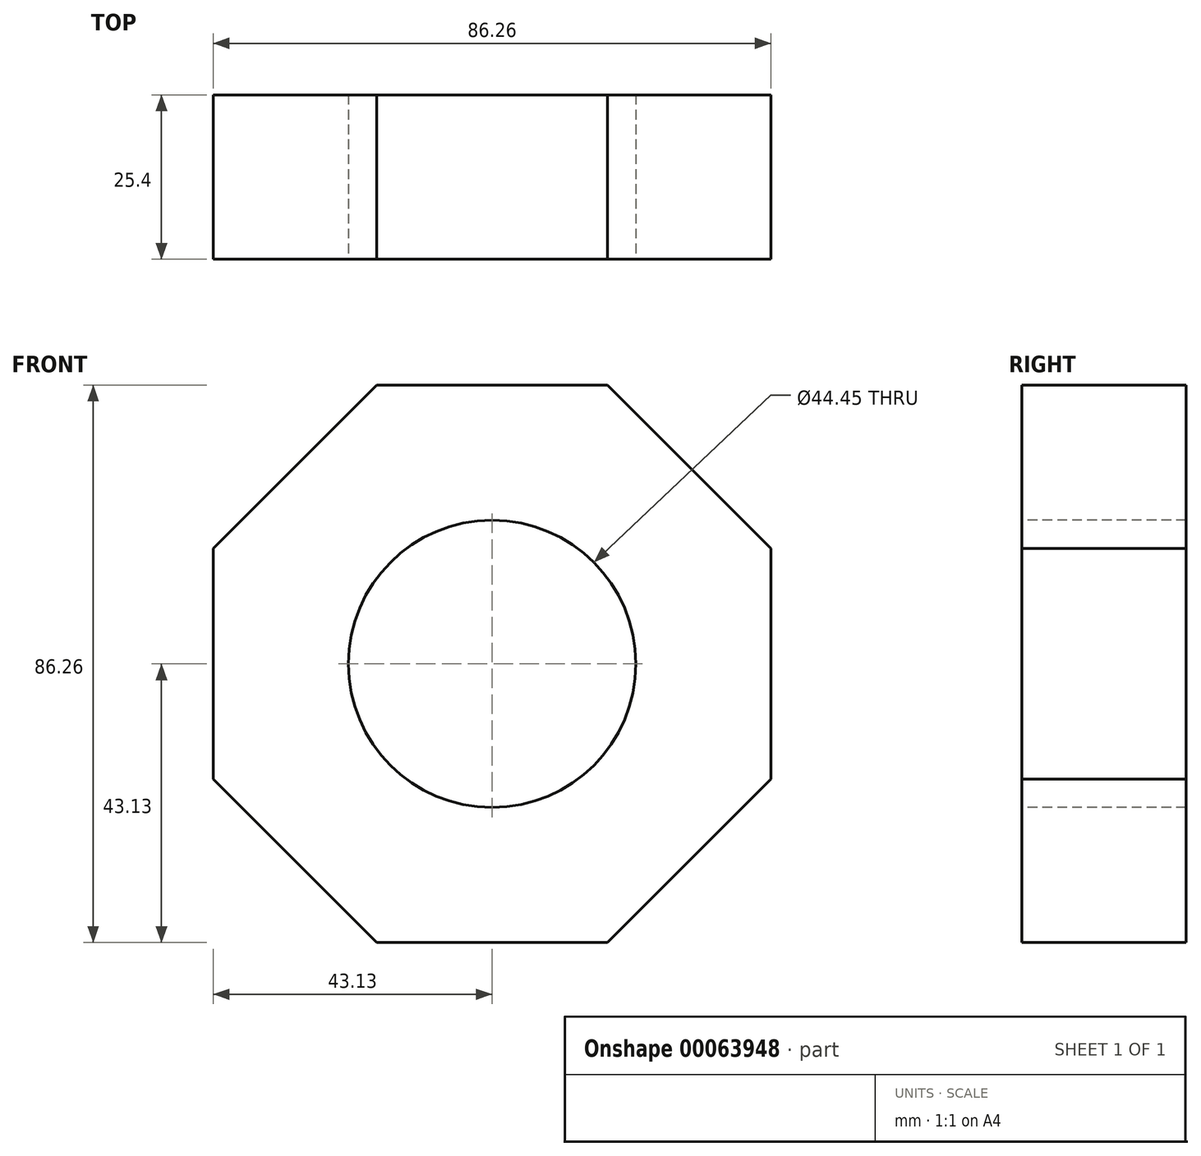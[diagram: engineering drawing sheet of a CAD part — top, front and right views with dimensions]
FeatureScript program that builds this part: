
annotation { "Feature Type Name" : "Feature", "Feature Type Description" : "" }
export const myFeature = defineFeature(function(context is Context, id is Id, definition is map)
    precondition{}
    {
        {
            var Q0;
            Q0=qCreatedBy(makeId("Front.planeOp"),FACE);
            var sketch = newSketch(context, id + "F0", { "sketchPlane" : qUnion([Q0])});
            skCircle(sketch, "E0.cCircle", {"center": v(0, 0) * mm, "radius": 43.13 * mm, "construction": true});
            skLineSegment(sketch, "E0.0", {"start": v(-17.86, 43.13) * mm, "end": v(17.86, 43.13) * mm});
            skLineSegment(sketch, "E0.1", {"start": v(17.86, 43.13) * mm, "end": v(43.13, 17.86) * mm});
            skLineSegment(sketch, "E0.2", {"start": v(43.13, 17.86) * mm, "end": v(43.13, -17.86) * mm});
            skLineSegment(sketch, "E0.3", {"start": v(43.13, -17.86) * mm, "end": v(17.86, -43.13) * mm});
            skLineSegment(sketch, "E0.4", {"start": v(17.86, -43.13) * mm, "end": v(-17.86, -43.13) * mm});
            skLineSegment(sketch, "E0.5", {"start": v(-17.86, -43.13) * mm, "end": v(-43.13, -17.86) * mm});
            skLineSegment(sketch, "E0.6", {"start": v(-43.13, -17.86) * mm, "end": v(-43.13, 17.86) * mm});
            skLineSegment(sketch, "E0.7", {"start": v(-43.13, 17.86) * mm, "end": v(-17.86, 43.13) * mm});
            skPoint(sketch, "E0.0.midPoint", {"position": v(0, 43.13) * mm});
            skSolve(sketch);
        }
        {
            var Q0;
            Q0 = qSketchRegion(id + "F0", true);
            extrude(context, id + "F1", {"entities" : qUnion([Q0]), "depth" : 25.4 * mm});
        }
        {
            var Q0;
            Q0=makeQuery(id+"F1.opExtrude","CAP_FACE",FACE,{"disambiguationData":[OSD([sQuery(id+"F0.wireOp",EDGE,"E0.0"),sQuery(id+"F0.wireOp",EDGE,"E0.1"),sQuery(id+"F0.wireOp",EDGE,"E0.2"),sQuery(id+"F0.wireOp",EDGE,"E0.3"),sQuery(id+"F0.wireOp",EDGE,"E0.4"),sQuery(id+"F0.wireOp",EDGE,"E0.5"),sQuery(id+"F0.wireOp",EDGE,"E0.6"),sQuery(id+"F0.wireOp",EDGE,"E0.7")])],"isStart":false});
            var sketch = newSketch(context, id + "F2", { "sketchPlane" : qUnion([Q0])});
            skCircle(sketch, "E1", {"center": v(0, 0) * mm, "radius": 20.45 * mm});
            skSolve(sketch);
        }
        {
            var Q0;
            Q0=sQuery(id+"F2.wireOp",VERTEX,"E1.center");
            var Q1;
            Q1=makeQuery(id+"F1.opExtrude","SWEPT_BODY",BODY,{"disambiguationData":[OSD([sQuery(id+"F0.wireOp",EDGE,"E0.0"),sQuery(id+"F0.wireOp",EDGE,"E0.1"),sQuery(id+"F0.wireOp",EDGE,"E0.2"),sQuery(id+"F0.wireOp",EDGE,"E0.3"),sQuery(id+"F0.wireOp",EDGE,"E0.4"),sQuery(id+"F0.wireOp",EDGE,"E0.5"),sQuery(id+"F0.wireOp",EDGE,"E0.6"),sQuery(id+"F0.wireOp",EDGE,"E0.7")])]});
            hole(context, id + "F3", {"style" : HoleStyle.SIMPLE, "holeDiameter" : 44.45 * mm, "endStyle" : HoleEndStyle.THROUGH, "locations" : qUnion([Q0]), "scope" : qUnion([Q1])});
        }
    });
